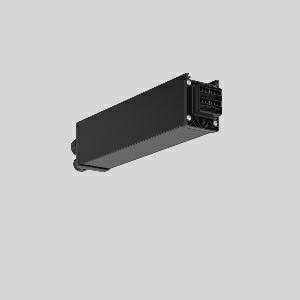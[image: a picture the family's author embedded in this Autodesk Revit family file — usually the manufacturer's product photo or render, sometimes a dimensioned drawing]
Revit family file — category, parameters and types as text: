
# Revit family: linedo_anfangseinspeisung_14pol_s_982678_003_1_4122
name_source: partatom
category: Lighting Fixtures
units: mm (PartAtom-declared; Revit-internal decimal feet)

## family parameters
Cut with Voids When Loaded = No
Host = Face
Light Source = No
Part Type = Normal
Room Calculation Point = No
Round Connector Dimension = Use Diameter
Shared = No

## types (1)
- LINEDO_Anfangseinspeisung_14pol_S
    Apparent Load = 0 VA
    Default Elevation = 1800 mm
    Description = Series: LINEDO
Initial power feed, 14-pole, connection plug. Housing: extruded aluminium profile, powder-coated. Cover made of plastic, surface like housing. LINEDO plug system, plastic, black. 2 cable glands (M20 and M25). Cable glands on side or on top. Easy connection for rigid or flexible wires.
Colour: black
Length: 330 mm
Width: 58 mm
Height: 76 mm
Weight: 728 g
    Height = 76 mm
    Lamp = 0 x
    Length = 330 mm
    Luminous efficacy = 0 lm/W
    Manufacturer = RZB
    ModVariant = No
    Model = 982678.003.1
    Mounting Place = Ceiling
    Mounting Type = Surface mounted, Pendant
    Number of Poles = 1
    OnlyDefault = Yes
    Power Factor = 1
    Product Name = LINEDO_Anfangseinspeisung_14pol_S
    Product group = Continuous line luminaire system Linedo IP 54
    ProductGroupID = 314
    Protection Class = Protection class I
    Protection Degree = IP 54
    RLX_Detail_Level = 1
    RLX_Emergency_Light_Flux = 0 lm
    RLX_Emergency_Type = 0
    RLX_Emergency_Type_DB = No
    RlxData = <blob elided: 14937 chars, md5=2ca37708>
    Standby Power = 0 W
    System Light Flux = 0 lm
    System Power = 0 W
    Type Comments = Product without accessories
    Type Image = 982678.003.1.jpg
    URL = http://relux.com
    VarID = ---
    Voltage = 0 V
    Weight = 0.00 kg
    Width = 58 mm

## geometry (parser evidence)
native form markers: Sweep x10
no freeform markers — native parametric forms only
